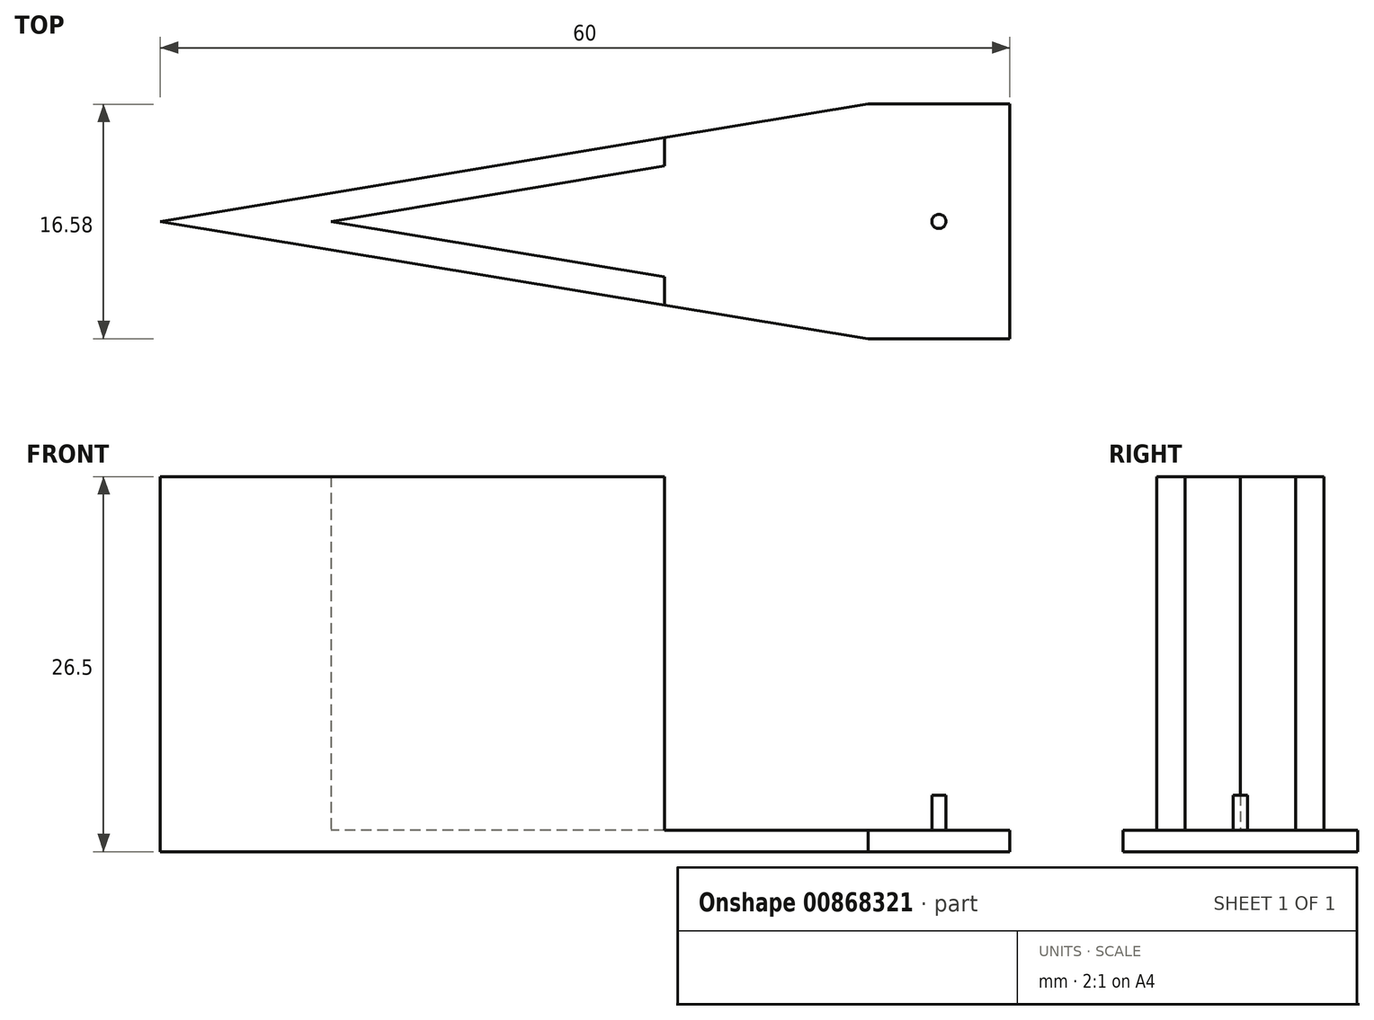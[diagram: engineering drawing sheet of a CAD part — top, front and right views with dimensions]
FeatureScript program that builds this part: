
annotation { "Feature Type Name" : "Feature", "Feature Type Description" : "" }
export const myFeature = defineFeature(function(context is Context, id is Id, definition is map)
    precondition{}
    {
        {
            var Q0;
            Q0=qCreatedBy(makeId("Top.planeOp"),FACE);
            var sketch = newSketch(context, id + "F0", { "sketchPlane" : qUnion([Q0])});
            skCircle(sketch, "E0", {"center": v(19.18, 26.22) * mm, "radius": 10 * mm, "construction": true});
            skLineSegment(sketch, "E1", {"start": v(29.17, 25.82) * mm, "end": v(26.17, 25.82) * mm, "construction": true});
            skLineSegment(sketch, "E2", {"start": v(26.17, 25.82) * mm, "end": v(26.17, 29.6) * mm});
            skLineSegment(sketch, "E3", {"start": v(26.17, 29.6) * mm, "end": v(26.17, 33.37) * mm});
            skLineSegment(sketch, "E4", {"start": v(26.17, 25.82) * mm, "end": v(26.17, 22.45) * mm});
            skLineSegment(sketch, "E5", {"start": v(26.17, 22.45) * mm, "end": v(26.17, 19.07) * mm});
            skLineSegment(sketch, "E6.bottom", {"start": v(12.46, -35.5) * mm, "end": v(22.46, -35.5) * mm});
            skLineSegment(sketch, "E6.top", {"start": v(12.46, -18.92) * mm, "end": v(22.46, -18.92) * mm});
            skLineSegment(sketch, "E6.right", {"start": v(22.46, -35.5) * mm, "end": v(22.46, -18.92) * mm});
            skLineSegment(sketch, "E7", {"start": v(12.46, -18.92) * mm, "end": v(12.46, -35.5) * mm, "construction": true});
            skLineSegment(sketch, "E8", {"start": v(17.46, -22.48) * mm, "end": v(17.46, -27.2) * mm, "construction": true});
            skLineSegment(sketch, "E9", {"start": v(17.46, -27.2) * mm, "end": v(17.46, -31.94) * mm, "construction": true});
            skLineSegment(sketch, "E10", {"start": v(12.46, -18.92) * mm, "end": v(-37.54, -27.2) * mm});
            skLineSegment(sketch, "E11", {"start": v(12.46, -35.5) * mm, "end": v(-37.54, -27.2) * mm});
            skLineSegment(sketch, "E12", {"start": v(12.46, -27.2) * mm, "end": v(-37.54, -27.2) * mm, "construction": true});
            skSolve(sketch);
        }
        {
            var Q0;
            Q0=makeQuery(id+"F0.imprint","IMPRINT",FACE,{"disambiguationData":[TD([[makeQuery(id+"F0.imprint","IMPRINT",EDGE,{"derivedFrom":sQuery(id+"F0.wireOp",EDGE,"E6.bottom")}),1.0]])]});
            extrude(context, id + "F1", {"entities" : qUnion([Q0]), "depth" : 1.5 * mm, "offsetDistance" : 25 * mm});
        }
        {
            var Q0;
            Q0=makeQuery(id+"F1.opExtrude","CAP_FACE",FACE,{"disambiguationData":[OSD([sQuery(id+"F0.wireOp",EDGE,"E6.bottom"),sQuery(id+"F0.wireOp",EDGE,"E6.top"),sQuery(id+"F0.wireOp",EDGE,"E6.right"),sQuery(id+"F0.wireOp",EDGE,"E10"),sQuery(id+"F0.wireOp",EDGE,"E11")])],"isStart":false});
            var sketch = newSketch(context, id + "F2", { "sketchPlane" : qUnion([Q0])});
            skLineSegment(sketch, "E13", {"start": v(-1.91, -33.12) * mm, "end": v(-1.91, -31.12) * mm});
            skLineSegment(sketch, "E14", {"start": v(-1.91, -21.3) * mm, "end": v(-1.91, -23.3) * mm});
            skLineSegment(sketch, "E15.trimOffspring", {"start": v(-1.91, -31.12) * mm, "end": v(-1.91, -33.12) * mm});
            skLineSegment(sketch, "E16", {"start": v(-37.54, -27.2) * mm, "end": v(-1.91, -21.3) * mm});
            skLineSegment(sketch, "E17", {"start": v(-1.91, -33.12) * mm, "end": v(-37.54, -27.2) * mm});
            skLineSegment(sketch, "E18", {"start": v(-1.91, -23.3) * mm, "end": v(-25.49, -27.2) * mm});
            skLineSegment(sketch, "E19", {"start": v(-25.49, -27.2) * mm, "end": v(-1.91, -31.12) * mm});
            skSolve(sketch);
        }
        {
            var Q0;
            Q0=makeQuery(id+"F2.imprint","IMPRINT",FACE,{"disambiguationData":[TD([[makeQuery(id+"F2.imprint","IMPRINT",EDGE,{"derivedFrom":sQuery(id+"F2.wireOp",EDGE,"vwf6Xuvv-GLHZ-b0TN-8YnZ-4lmlUbzJXBV8")}),1.0]])]});
            var Q1;
            Q1=makeQuery(id+"F2.imprint","IMPRINT",FACE,{"disambiguationData":[TD([[makeQuery(id+"F2.imprint","IMPRINT",EDGE,{"derivedFrom":sQuery(id+"F2.wireOp",EDGE,"E14")}),-1.0]])]});
            var Q2;
            {var subQ0=sQuery(id+"F2.wireOp",EDGE,"A1KeINGd-nCUG-whud-7RbA-fV79oP6xntIB");Q2=makeQuery(id+"F2.imprint","IMPRINT",FACE,{"disambiguationData":[TD([[makeQuery(id+"F2.imprint","IMPRINT",EDGE,{"derivedFrom":subQ0}),-1.0]])]});}
            var Q3;
            Q3=makeQuery(id+"F2.imprint","IMPRINT",FACE,{"disambiguationData":[TD([[makeQuery(id+"F2.imprint","IMPRINT",EDGE,{"derivedFrom":sQuery(id+"F2.wireOp",EDGE,"E14")}),-1.0]])]});
            var Q4;
            Q4 = qSketchRegion(id + "F4", true);
            extrude(context, id + "F3", {"entities" : qUnion([Q0, Q1, Q2, Q3, Q4]), "operationType" : NewBodyOperationType.ADD, "depth" : 25 * mm, "offsetDistance" : 25 * mm});
        }
        {
            var Q0;
            Q0=makeQuery(id+"F1.opExtrude","CAP_FACE",FACE,{"disambiguationData":[OSD([sQuery(id+"F0.wireOp",EDGE,"E6.bottom"),sQuery(id+"F0.wireOp",EDGE,"E6.top"),sQuery(id+"F0.wireOp",EDGE,"E6.right"),sQuery(id+"F0.wireOp",EDGE,"E10"),sQuery(id+"F0.wireOp",EDGE,"E11")])],"isStart":false});
            var sketch = newSketch(context, id + "F4", { "sketchPlane" : qUnion([Q0])});
            skLineSegment(sketch, "E20", {"start": v(17.46, -18.92) * mm, "end": v(17.46, -35.5) * mm, "construction": true});
            skLineSegment(sketch, "E21", {"start": v(17.46, -35.5) * mm, "end": v(17.46, -23.83) * mm, "construction": true});
            skLineSegment(sketch, "E22", {"start": v(17.46, -23.83) * mm, "end": v(17.46, -27.2) * mm, "construction": true});
            skLineSegment(sketch, "E23", {"start": v(17.46, -27.2) * mm, "end": v(17.46, -30.58) * mm, "construction": true});
            skCircle(sketch, "E24", {"center": v(17.46, -27.2) * mm, "radius": 0.5 * mm});
            skSolve(sketch);
        }
        {
            var Q0;
            Q0=makeQuery(id+"F4.imprint","IMPRINT",FACE,{"disambiguationData":[TD([[makeQuery(id+"F4.imprint","IMPRINT",EDGE,{"derivedFrom":sQuery(id+"F4.wireOp",EDGE,"E24")}),1.0]])]});
            var Q1;
            Q1=makeQuery(id+"F4.imprint","IMPRINT",FACE,{"disambiguationData":[TD([[makeQuery(id+"F4.imprint","IMPRINT",EDGE,{"derivedFrom":sQuery(id+"F4.wireOp",EDGE,"lBZs4Hom-cFyz-wjp9-qYjC-MN7P4qM1fXig")}),1.0]])]});
            var Q2;
            Q2=makeQuery(id+"F4.imprint","IMPRINT",FACE,{"disambiguationData":[TD([[makeQuery(id+"F4.imprint","IMPRINT",EDGE,{"derivedFrom":sQuery(id+"F4.wireOp",EDGE,"xrMoSdof-7EzX-8pLs-IOM9-xb4upInqfTwY")}),1.0]])]});
            extrude(context, id + "F5", {"entities" : qUnion([Q0, Q1, Q2]), "operationType" : NewBodyOperationType.ADD, "depth" : 2.5 * mm, "offsetDistance" : 25 * mm});
        }
    });
